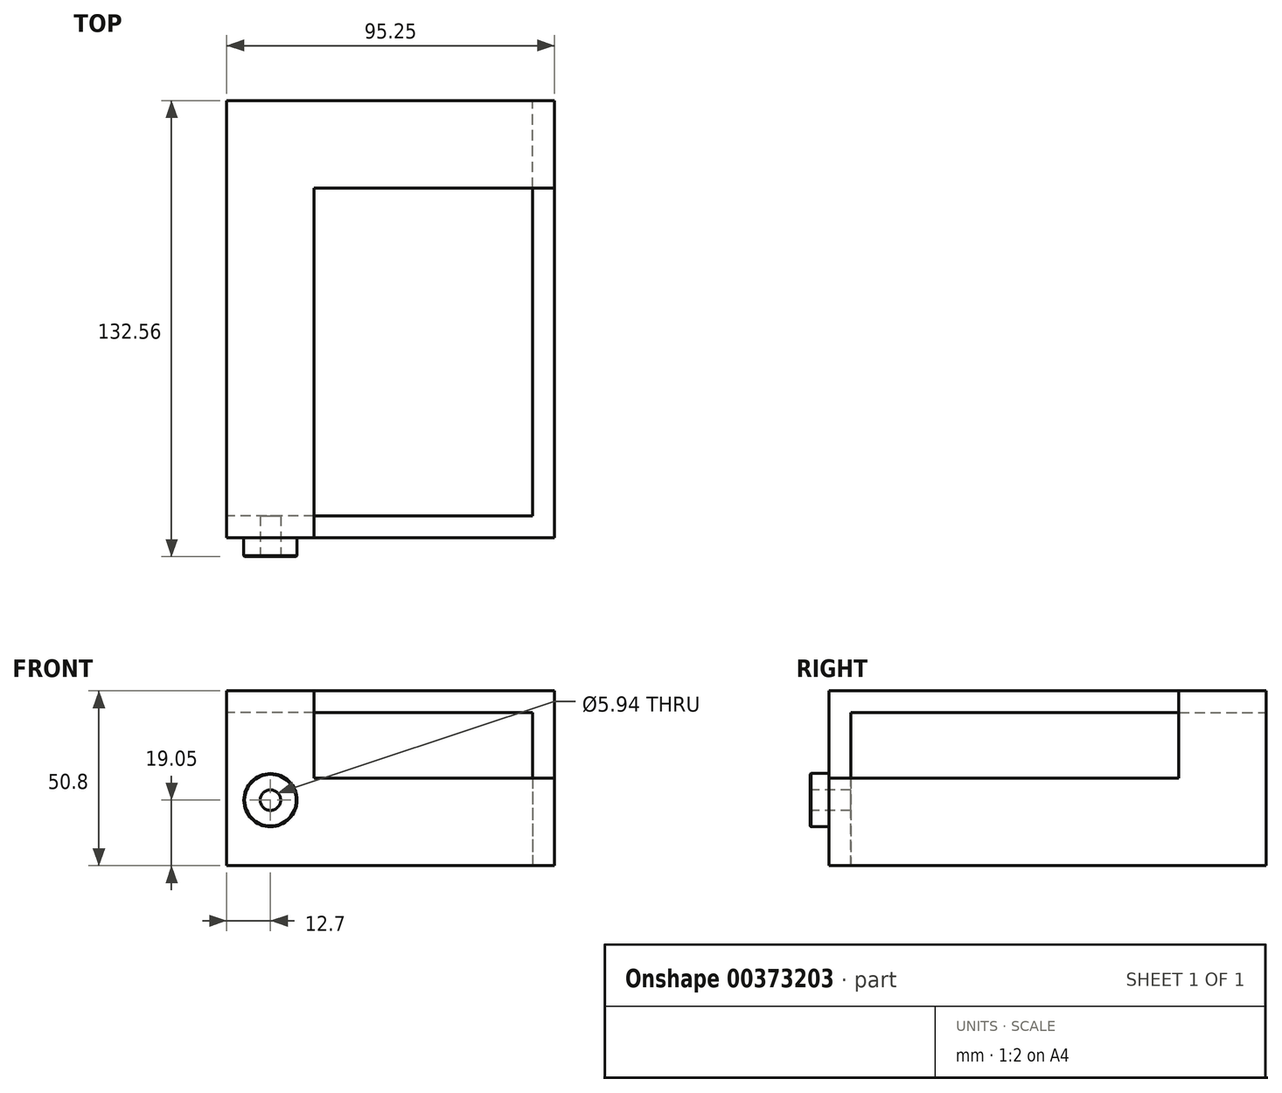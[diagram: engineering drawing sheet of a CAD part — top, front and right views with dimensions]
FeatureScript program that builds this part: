
annotation { "Feature Type Name" : "Feature", "Feature Type Description" : "" }
export const myFeature = defineFeature(function(context is Context, id is Id, definition is map)
    precondition{}
    {
        {
            var Q0;
            Q0=qCreatedBy(makeId("Right.planeOp"),FACE);
            var sketch = newSketch(context, id + "F0", { "sketchPlane" : qUnion([Q0])});
            skLineSegment(sketch, "E0", {"start": v(120.65, 31.75) * mm, "end": v(-6.35, 31.75) * mm});
            skLineSegment(sketch, "E1", {"start": v(-6.35, 31.75) * mm, "end": v(-6.35, -19.05) * mm});
            skLineSegment(sketch, "E2", {"start": v(-6.35, -19.05) * mm, "end": v(0, -19.05) * mm});
            skLineSegment(sketch, "E3", {"start": v(0, -19.05) * mm, "end": v(0, 25.4) * mm});
            skLineSegment(sketch, "E4", {"start": v(0, 25.4) * mm, "end": v(120.65, 25.4) * mm});
            skLineSegment(sketch, "E5", {"start": v(120.65, 25.4) * mm, "end": v(120.65, 31.75) * mm});
            skSolve(sketch);
        }
        {
            var Q0;
            Q0 = qSketchRegion(id + "F0", true);
            extrude(context, id + "F1", {"entities" : qUnion([Q0]), "depth" : 12.7 * mm, "hasSecondDirection" : true, "secondDirectionOppositeDirection" : true, "secondDirectionDepth" : 12.7 * mm});
        }
        {
            var Q0;
            Q0=makeQuery(id+"F1.opExtrude","SWEPT_FACE",FACE,{"disambiguationData":[OSD([sQuery(id+"F0.wireOp",EDGE,"E2")])]});
            var sketch = newSketch(context, id + "F2", { "sketchPlane" : qUnion([Q0])});
            skLineSegment(sketch, "E6", {"start": v(12.7, 0) * mm, "end": v(12.7, 6.35) * mm});
            skLineSegment(sketch, "E7", {"start": v(12.7, 6.35) * mm, "end": v(82.55, 6.35) * mm});
            skLineSegment(sketch, "E8", {"start": v(82.55, 6.35) * mm, "end": v(82.55, -120.65) * mm});
            skLineSegment(sketch, "E9", {"start": v(82.55, -120.65) * mm, "end": v(76.2, -120.65) * mm});
            skLineSegment(sketch, "E10", {"start": v(76.2, -120.65) * mm, "end": v(76.2, 0) * mm});
            skLineSegment(sketch, "E11", {"start": v(76.2, 0) * mm, "end": v(12.7, 0) * mm});
            skSolve(sketch);
        }
        {
            var Q0;
            Q0 = qSketchRegion(id + "F2", true);
            extrude(context, id + "F3", {"entities" : qUnion([Q0]), "operationType" : NewBodyOperationType.ADD, "oppositeDirection" : true, "depth" : 25.4 * mm});
        }
        {
            var Q0;
            Q0=makeQuery(id+"F1.opExtrude","SWEPT_FACE",FACE,{"disambiguationData":[OSD([sQuery(id+"F0.wireOp",EDGE,"E5")])]});
            var sketch = newSketch(context, id + "F4", { "sketchPlane" : qUnion([Q0])});
            skLineSegment(sketch, "E12", {"start": v(-12.7, 31.75) * mm, "end": v(-82.55, 31.75) * mm});
            skLineSegment(sketch, "E13", {"start": v(-82.55, 31.75) * mm, "end": v(-82.55, 6.35) * mm});
            skLineSegment(sketch, "E14", {"start": v(-82.55, 6.35) * mm, "end": v(-76.2, 6.35) * mm});
            skLineSegment(sketch, "E15", {"start": v(-76.2, 6.35) * mm, "end": v(-76.2, 25.4) * mm});
            skLineSegment(sketch, "E16", {"start": v(-76.2, 25.4) * mm, "end": v(-12.7, 25.4) * mm});
            skLineSegment(sketch, "E17", {"start": v(-12.7, 25.4) * mm, "end": v(-12.7, 31.75) * mm});
            skSolve(sketch);
        }
        {
            var Q0;
            Q0 = qSketchRegion(id + "F4", true);
            extrude(context, id + "F5", {"entities" : qUnion([Q0]), "operationType" : NewBodyOperationType.ADD, "oppositeDirection" : true, "depth" : 25.4 * mm});
        }
        {
            var Q0;
            Q0=makeQuery(id+"F1.opExtrude","SWEPT_FACE",FACE,{"disambiguationData":[OSD([sQuery(id+"F0.wireOp",EDGE,"E1")])]});
            var sketch = newSketch(context, id + "F6", { "sketchPlane" : qUnion([Q0])});
            skCircle(sketch, "E18", {"center": v(0, 0) * mm, "radius": 6.35 * mm});
            skSolve(sketch);
        }
        {
            var Q0;
            Q0 = qSketchRegion(id + "F6", true);
            extrude(context, id + "F7", {"entities" : qUnion([Q0]), "operationType" : NewBodyOperationType.REMOVE, "endBound" : BoundingType.UP_TO_NEXT, "oppositeDirection" : true, "depth" : 25.4 * mm});
        }
        {
            var Q0;
            Q0=makeQuery(id+"F1.opExtrude","SWEPT_FACE",FACE,{"disambiguationData":[OSD([sQuery(id+"F0.wireOp",EDGE,"E1")])]});
            var sketch = newSketch(context, id + "F8", { "sketchPlane" : qUnion([Q0])});
            skCircle(sketch, "E19.0", {"center": v(0, 0) * mm, "radius": 6.35 * mm});
            skCircle(sketch, "E20", {"center": v(0, 0) * mm, "radius": 2.97 * mm});
            skSolve(sketch);
        }
        {
            var Q0;
            Q0 = qSketchRegion(id + "F8", true);
            extrude(context, id + "F9", {"entities" : qUnion([Q0]), "oppositeDirection" : true, "depth" : 6.35 * mm});
        }
        {
            var Q0;
            Q0=makeQuery(id+"F9.opExtrude","CAP_FACE",FACE,{"disambiguationData":[OSD([sQuery(id+"F8.wireOp",EDGE,"E19.0"),sQuery(id+"F8.wireOp",EDGE,"E20")])],"isStart":true});
            var sketch = newSketch(context, id + "F10", { "sketchPlane" : qUnion([Q0])});
            skCircle(sketch, "E21.1", {"center": v(0, 0) * mm, "radius": 2.97 * mm});
            skCircle(sketch, "E22", {"center": v(0, 0) * mm, "radius": 7.74 * mm});
            skSolve(sketch);
        }
        {
            var Q0;
            Q0 = qSketchRegion(id + "F10", true);
            extrude(context, id + "F11", {"entities" : qUnion([Q0]), "operationType" : NewBodyOperationType.ADD, "depth" : 5.56 * mm});
        }
        {
            var Q0;
            Q0=makeQuery(id+"F11.opExtrude","CAP_EDGE",EDGE,{"disambiguationData":[OSD([sQuery(id+"F10.wireOp",EDGE,"E21.1")])],"isStart":false});
            fillet(context, id + "F12", {"entities" : qUnion([Q0]), "radius" : 0.76 * mm, "tangentPropagation" : true, "allowEdgeOverflow" : false});
        }
        {
            var Q0;
            Q0=makeQuery(id+"F11.opExtrude","CAP_EDGE",EDGE,{"disambiguationData":[OSD([sQuery(id+"F10.wireOp",EDGE,"E22")])],"isStart":false});
            chamfer(context, id + "F13", {"entities" : qUnion([Q0]), "width" : 0.25 * mm, "tangentPropagation" : true});
        }
    });
